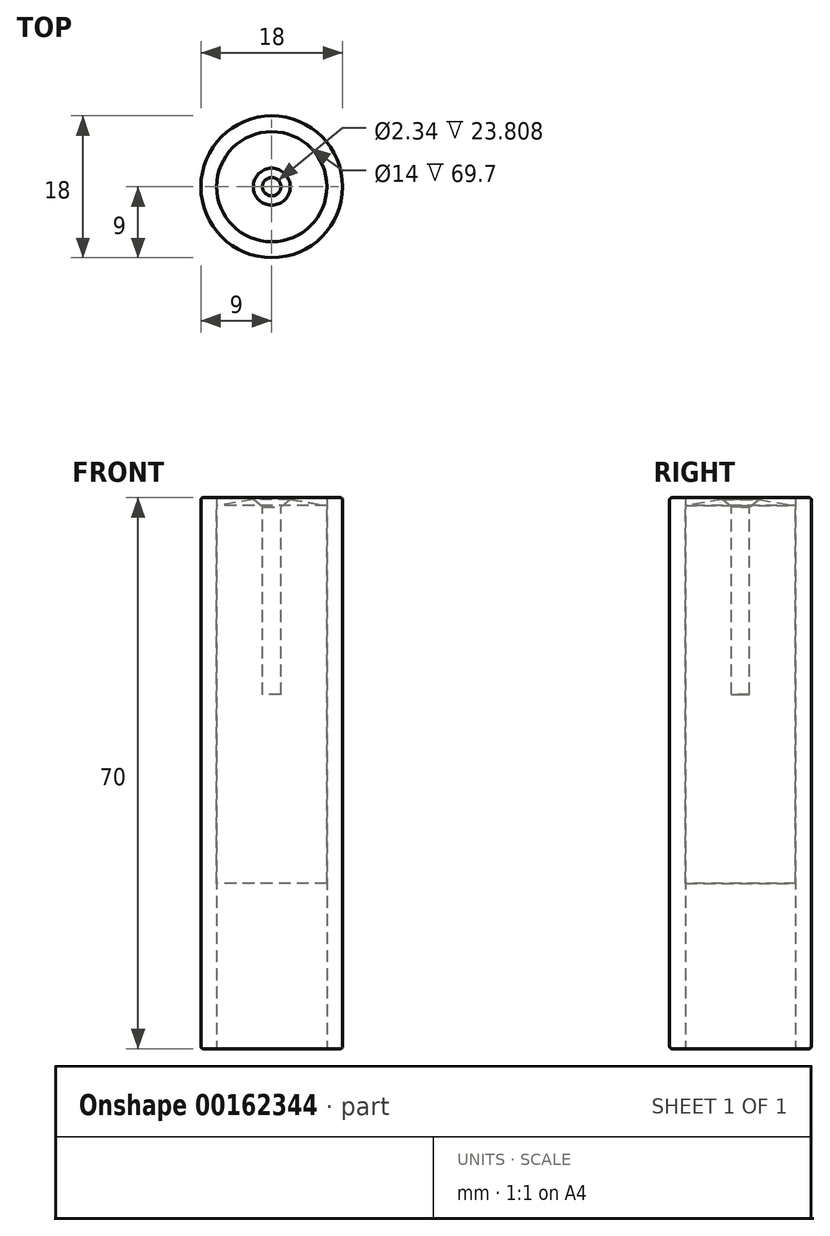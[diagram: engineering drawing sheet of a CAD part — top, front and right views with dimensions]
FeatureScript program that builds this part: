
annotation { "Feature Type Name" : "Feature", "Feature Type Description" : "" }
export const myFeature = defineFeature(function(context is Context, id is Id, definition is map)
    precondition{}
    {
        {
            var Q0;
            Q0=qCreatedBy(makeId("Top.planeOp"),FACE);
            var sketch = newSketch(context, id + "F0", { "sketchPlane" : qUnion([Q0])});
            skCircle(sketch, "E0", {"center": v(0, 0) * mm, "radius": 9 * mm});
            skCircle(sketch, "E1", {"center": v(0, 0) * mm, "radius": 7 * mm});
            skSolve(sketch);
        }
        {
            var Q0;
            Q0 = qSketchRegion(id + "F0", true);
            extrude(context, id + "F1", {"entities" : qUnion([Q0]), "depth" : 70 * mm});
        }
        {
            var Q0;
            Q0=qCreatedBy(makeId("Right.planeOp"),FACE);
            var sketch = newSketch(context, id + "F2", { "sketchPlane" : qUnion([Q0])});
            skLineSegment(sketch, "E2.0", {"start": v(-7, 70) * mm, "end": v(7, 70) * mm, "construction": true});
            skLineSegment(sketch, "E3", {"start": v(7, 68.97) * mm, "end": v(1.17, 70) * mm});
            skLineSegment(sketch, "E4", {"start": v(1.17, 70) * mm, "end": v(0, 70) * mm});
            skLineSegment(sketch, "E5", {"start": v(0, 70) * mm, "end": v(0, 20.97) * mm, "construction": true});
            skLineSegment(sketch, "E6.MirrorCS", {"start": v(-1.17, 70) * mm, "end": v(0, 70) * mm});
            skLineSegment(sketch, "E7", {"start": v(7, 68.97) * mm, "end": v(7, 20.97) * mm});
            skLineSegment(sketch, "E8", {"start": v(7, 20.97) * mm, "end": v(0, 20.97) * mm});
            skLineSegment(sketch, "E9", {"start": v(0, 70) * mm, "end": v(0, 20.97) * mm});
            skSolve(sketch);
        }
        {
            var Q0;
            Q0 = qSketchRegion(id + "F2", true);
            var Q1;
            Q1=sQuery(id+"F2.wireOp",EDGE,"E5");
            revolve(context, id + "F3", {"entities" : qUnion([Q0]), "axis" : qUnion([Q1]), "revolveType" : RevolveType.FULL});
        }
        {
            var Q0;
            Q0=makeQuery(id+"F3.opRevolve","SWEPT_FACE",FACE,{"disambiguationData":[OSD([sQuery(id+"F2.wireOp",EDGE,"E4")])]});
            extrude(context, id + "F4", {"entities" : qUnion([Q0]), "operationType" : NewBodyOperationType.REMOVE, "oppositeDirection" : true, "depth" : 25 * mm});
        }
        {
            var Q0;
            {var subQ0=sQuery(id+"F2.wireOp",EDGE,"E4");var subQ1=sQuery(id+"F2.wireOp",EDGE,"E3");Q0=makeQuery(id+"F4.boolean.opBoolean","MERGE",EDGE,{"derivedFrom":[makeQuery(id+"F3.opRevolve","SWEPT_EDGE",EDGE,{"disambiguationData":[OSD([subQ1,subQ0])]}),makeQuery(id+"F4.opExtrude","CAP_EDGE",EDGE,{"disambiguationData":[OSD([subQ1,subQ0])],"isStart":true})]});}
            chamfer(context, id + "F5", {"entities" : qUnion([Q0]), "width" : 1 * mm, "tangentPropagation" : true});
        }
        {
            var Q0;
            Q0=makeQuery(id+"F1.opExtrude","CAP_EDGE",EDGE,{"disambiguationData":[OSD([sQuery(id+"F0.wireOp",EDGE,"E0")])],"isStart":false});
            var Q1;
            Q1=makeQuery(id+"F1.opExtrude","CAP_EDGE",EDGE,{"disambiguationData":[OSD([sQuery(id+"F0.wireOp",EDGE,"E0")])],"isStart":true});
            var Q2;
            Q2=makeQuery(id+"F1.opExtrude","CAP_EDGE",EDGE,{"disambiguationData":[OSD([sQuery(id+"F0.wireOp",EDGE,"E1")])],"isStart":true});
            fillet(context, id + "F6", {"entities" : qUnion([Q0, Q1, Q2]), "radius" : 0.3 * mm, "tangentPropagation" : true, "allowEdgeOverflow" : false});
        }
    });
